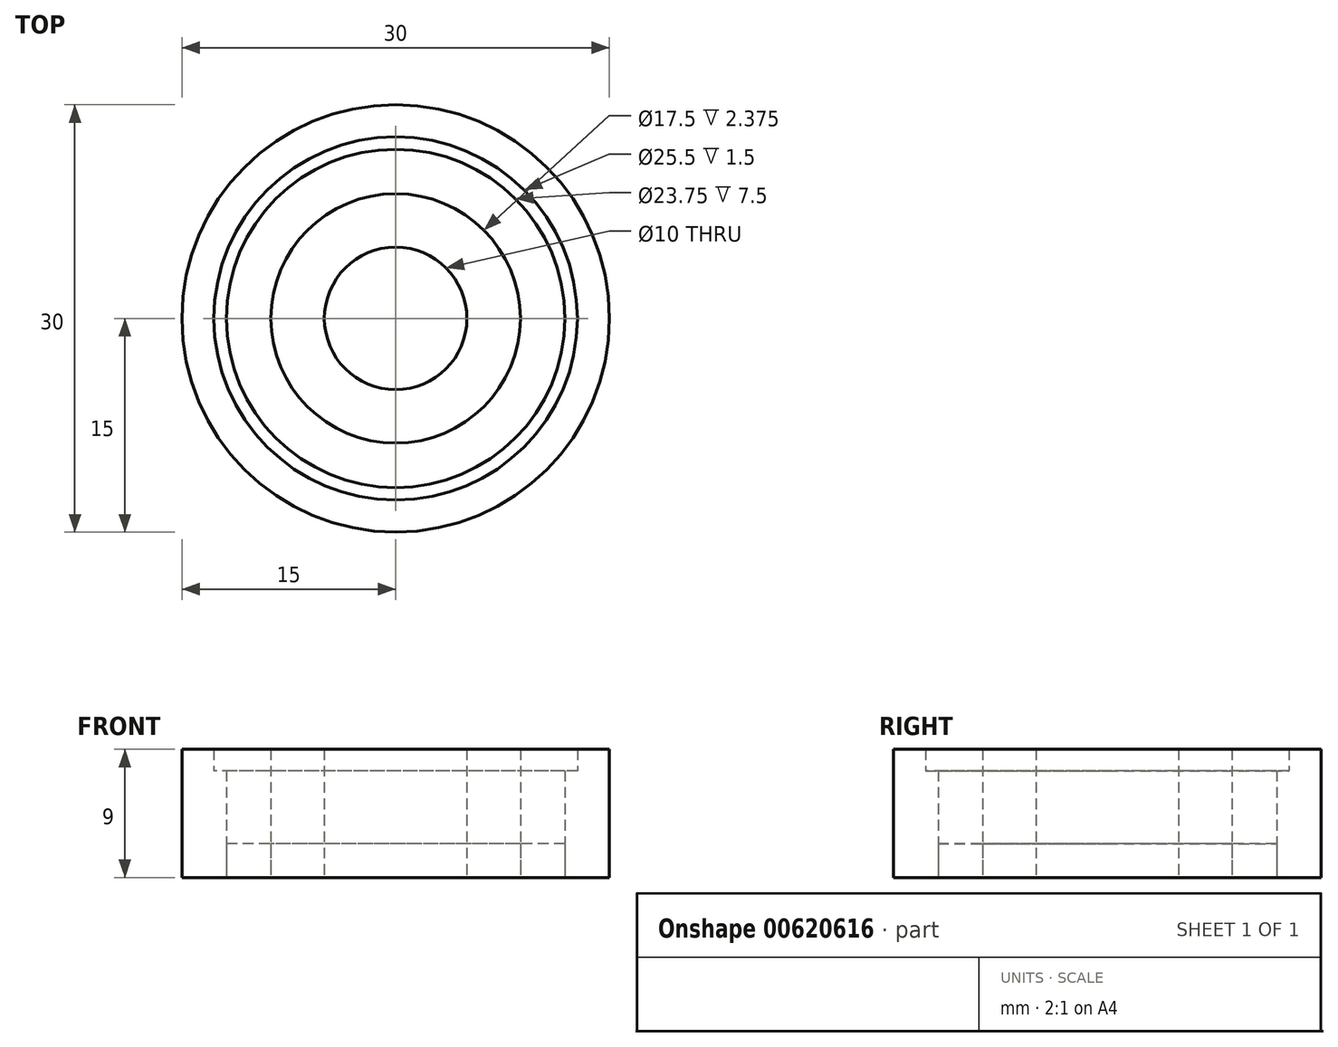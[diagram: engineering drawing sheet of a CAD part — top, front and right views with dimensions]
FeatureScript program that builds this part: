
annotation { "Feature Type Name" : "Feature", "Feature Type Description" : "" }
export const myFeature = defineFeature(function(context is Context, id is Id, definition is map)
    precondition{}
    {
        {
            var Q0;
            Q0=qCreatedBy(makeId("Top.planeOp"),FACE);
            var sketch = newSketch(context, id + "F0", { "sketchPlane" : qUnion([Q0])});
            skCircle(sketch, "E0", {"center": v(0, 0) * mm, "radius": 15 * mm});
            skCircle(sketch, "E1", {"center": v(0, 0) * mm, "radius": 12.75 * mm});
            skCircle(sketch, "E2", {"center": v(0, 0) * mm, "radius": 11.87 * mm});
            skCircle(sketch, "E3", {"center": v(0, 0) * mm, "radius": 8.75 * mm});
            skCircle(sketch, "E4", {"center": v(0, 0) * mm, "radius": 5 * mm});
            skSolve(sketch);
        }
        {
            var Q0;
            Q0=makeQuery(id+"F0.imprint","IMPRINT",FACE,{"disambiguationData":[TD([[makeQuery(id+"F0.imprint","IMPRINT",EDGE,{"derivedFrom":sQuery(id+"F0.wireOp",EDGE,"E0")}),1.0]])]});
            var Q1;
            Q1=makeQuery(id+"F0.imprint","IMPRINT",FACE,{"disambiguationData":[TD([[makeQuery(id+"F0.imprint","IMPRINT",EDGE,{"derivedFrom":sQuery(id+"F0.wireOp",EDGE,"E3")}),1.0]])]});
            extrude(context, id + "F1", {"entities" : qUnion([Q0, Q1]), "depth" : 9 * mm, "offsetDistance" : 25 * mm});
        }
        {
            var Q0;
            Q0=makeQuery(id+"F0.imprint","IMPRINT",FACE,{"disambiguationData":[TD([[makeQuery(id+"F0.imprint","IMPRINT",EDGE,{"derivedFrom":sQuery(id+"F0.wireOp",EDGE,"E1")}),1.0]])]});
            extrude(context, id + "F2", {"entities" : qUnion([Q0]), "operationType" : NewBodyOperationType.ADD, "depth" : 7.5 * mm, "offsetDistance" : 25 * mm});
        }
        {
            var Q0;
            Q0=makeQuery(id+"F0.imprint","IMPRINT",FACE,{"disambiguationData":[TD([[makeQuery(id+"F0.imprint","IMPRINT",EDGE,{"derivedFrom":sQuery(id+"F0.wireOp",EDGE,"E2")}),1.0]])]});
            extrude(context, id + "F3", {"entities" : qUnion([Q0]), "depth" : 2.38 * mm, "offsetDistance" : 25 * mm});
        }
    });
